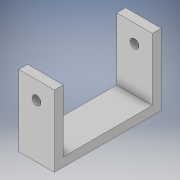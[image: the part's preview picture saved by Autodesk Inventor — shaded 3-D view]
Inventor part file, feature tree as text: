
AUTODESK INVENTOR PART (.ipt)
format: ipt  version: 2017 (Build 210142000, 142)  size: 110,080 bytes
history: native  units: in
note: dims shown in document units (in); Inventor stores cm internally (conversion verified against a paired STEP export)
features: sketch x2, extrude x1, hole x1, projected_geometry x1
ambient origin geometry x8: Origin, YZ Plane, XZ Plane, XY Plane, X Axis, Y Axis, Z Axis, Center Point
bodies: Solid1 (feature_tree)
feature tree (5):
  extrude  "Extrusion1"  Depth=3.0in
  hole  "Hole1"  [1 undecoded]
  sketch  "Sketch1"  dims[d0=2.0in d1=3.0in]
  sketch  "Sketch2"  dims[d2=0.25in d3=0.25in d4=0.25in d5=1.0in d6=0.0in d7=0.5in d8=0.5in d9=0.25in d10=0.75in d11=0.375in d12=0.25in d13=0.5635in d14=1.0in d15=0.8108in]
  projected_geometry  "Projected Loop1"
note: 1 required parameter value undecoded (feature->parameter linkage not recoverable at this tier; creation-order binding heuristic only, values carry confidence <= 0.55)
